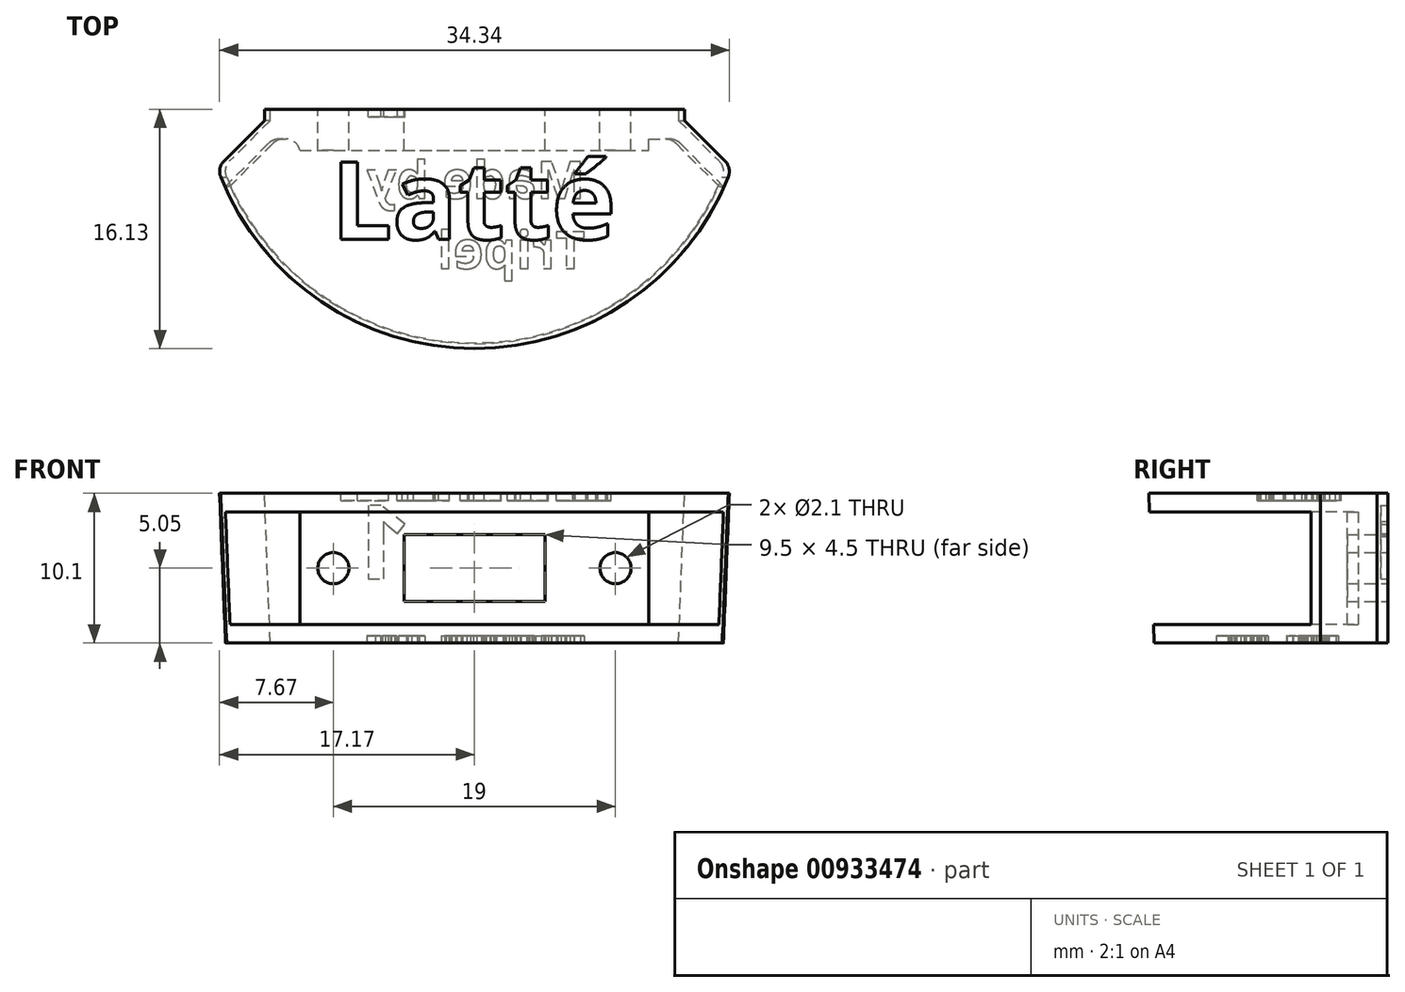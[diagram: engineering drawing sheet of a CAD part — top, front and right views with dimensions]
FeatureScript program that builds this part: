
annotation { "Feature Type Name" : "Feature", "Feature Type Description" : "" }
export const myFeature = defineFeature(function(context is Context, id is Id, definition is map)
    precondition{}
    {
        {
            assignVariable(context, id + "F0", {"variableType" : VariableType.LENGTH, "name" : "SwitchW", "lengthValue" : 7.6 * mm});
        }
        {
            assignVariable(context, id + "F1", {"variableType" : VariableType.LENGTH, "name" : "TopT", "lengthValue" : 2 * mm});
        }
        {
            assignVariable(context, id + "F2", {"variableType" : VariableType.LENGTH, "name" : "SideT", "lengthValue" : 1.25 * mm});
        }
        {
            var Q0;
            Q0=qCreatedBy(makeId("Top.planeOp"),FACE);
            var sketch = newSketch(context, id + "F3", { "sketchPlane" : qUnion([Q0])});
            skLineSegment(sketch, "E0", {"start": v(-13.75, 0) * mm, "end": v(13.75, 0) * mm});
            skPoint(sketch, "E1", {"position": v(0, 0) * mm});
            skLineSegment(sketch, "E2", {"start": v(-13.75, 0) * mm, "end": v(-16.93, -3.18) * mm});
            skLineSegment(sketch, "E3", {"start": v(13.75, 0) * mm, "end": v(16.93, -3.18) * mm});
            skArc(sketch, "E4", {"start": v(-16.93, -3.18) * mm, "mid": v(0, -15) * mm, "end": v(16.93, -3.18) * mm});
            skSolve(sketch);
        }
        {
            var Q0;
            Q0=qCreatedBy(makeId("Top.planeOp"),FACE);
            cPlane(context, id + "F4", {"entities" : qUnion([Q0]), "cplaneType" : CPlaneType.OFFSET, "offset" : getVariable(context, 'SwitchW') + (2 * getVariable(context, 'SideT')), "width" : 150 * mm, "height" : 150 * mm});
        }
        {
            var Q0;
            Q0=qCreatedBy(id+"F4.planeOp",FACE);
            var sketch = newSketch(context, id + "F5", { "sketchPlane" : qUnion([Q0])});
            skLineSegment(sketch, "E5.0", {"start": v(-14.15, 0) * mm, "end": v(14.15, 0) * mm});
            skLineSegment(sketch, "E6", {"start": v(-14.15, 0) * mm, "end": v(-17.33, -3.18) * mm});
            skLineSegment(sketch, "E7", {"start": v(14.15, 0) * mm, "end": v(17.33, -3.18) * mm});
            skArc(sketch, "E8.0", {"start": v(-16.93, -3.18) * mm, "mid": v(0, -15) * mm, "end": v(16.93, -3.18) * mm, "construction": true});
            skArc(sketch, "E9.0", {"start": v(-17.33, -3.18) * mm, "mid": v(0, -15.38) * mm, "end": v(17.33, -3.18) * mm});
            skSolve(sketch);
        }
        {
            var Q0;
            Q0 = qSketchRegion(id + "F3", true);
            var Q1;
            Q1 = qSketchRegion(id + "F5", true);
            loft(context, id + "F6", {"sheetProfilesArray" : [{ "sheetProfileEntities" : qUnion([Q0]) }, { "sheetProfileEntities" : qUnion([Q1]) }]});
        }
        {
            var Q0;
            Q0=makeQuery(id+"F6.opLoft","SWEPT_FACE",FACE,{"disambiguationData":[OSD([sQuery(id+"F3.wireOp",EDGE,"E2"),sQuery(id+"F3.wireOp",EDGE,"E3"),sQuery(id+"F3.wireOp",EDGE,"E4"),sQuery(id+"F5.wireOp",EDGE,"E6"),sQuery(id+"F5.wireOp",EDGE,"E7"),sQuery(id+"F5.wireOp",EDGE,"E9.0")])]});
            shell(context, id + "F7", {"entities" : qUnion([Q0]), "thickness" : getVariable(context, 'SideT')});
        }
        {
            var Q0;
            Q0=makeQuery(id+"F7.opShell","OFFSET_FACE",FACE,{"disambiguationData":[OSD([sQuery(id+"F3.wireOp",EDGE,"E0"),sQuery(id+"F3.wireOp",EDGE,"E2"),sQuery(id+"F3.wireOp",EDGE,"E3"),sQuery(id+"F5.wireOp",EDGE,"E5.0"),sQuery(id+"F5.wireOp",EDGE,"E6"),sQuery(id+"F5.wireOp",EDGE,"E7")])]});
            var sketch = newSketch(context, id + "F8", { "sketchPlane" : qUnion([Q0])});
            skLineSegment(sketch, "E10.0", {"start": v(11.75, 1.25) * mm, "end": v(-11.75, 1.25) * mm});
            skLineSegment(sketch, "E11.0", {"start": v(11.75, 8.85) * mm, "end": v(-11.75, 8.85) * mm});
            skPoint(sketch, "E12.orphan", {"position": v(-13.58, 8.85) * mm});
            skPoint(sketch, "E13.orphan", {"position": v(-14.15, 10.1) * mm});
            skPoint(sketch, "E14.orphan", {"position": v(-13.28, 1.25) * mm});
            skPoint(sketch, "E15.orphan", {"position": v(-13.75, 0) * mm});
            skPoint(sketch, "E16.orphan", {"position": v(13.58, 8.85) * mm});
            skPoint(sketch, "E17.orphan", {"position": v(14.15, 10.1) * mm});
            skPoint(sketch, "E18.orphan", {"position": v(13.28, 1.25) * mm});
            skPoint(sketch, "E19.orphan", {"position": v(13.75, 0) * mm});
            skPoint(sketch, "E20", {"position": v(0, 1.25) * mm});
            skLineSegment(sketch, "E21", {"start": v(-11.75, 1.25) * mm, "end": v(-11.75, 8.85) * mm});
            skLineSegment(sketch, "E22", {"start": v(11.75, 8.85) * mm, "end": v(11.75, 1.25) * mm});
            skSolve(sketch);
        }
        {
            var Q0;
            Q0 = qSketchRegion(id + "F8", true);
            extrude(context, id + "F9", {"entities" : qUnion([Q0]), "operationType" : NewBodyOperationType.ADD, "depth" : getVariable(context, 'TopT') - getVariable(context, 'SideT'), "offsetDistance" : 25 * mm});
        }
        {
            var Q0;
            Q0=makeQuery(id+"F6.opLoft","SWEPT_FACE",FACE,{"disambiguationData":[OSD([sQuery(id+"F3.wireOp",EDGE,"E0"),sQuery(id+"F3.wireOp",EDGE,"E2"),sQuery(id+"F3.wireOp",EDGE,"E3"),sQuery(id+"F5.wireOp",EDGE,"E5.0"),sQuery(id+"F5.wireOp",EDGE,"E6"),sQuery(id+"F5.wireOp",EDGE,"E7")])]});
            var sketch = newSketch(context, id + "F10", { "sketchPlane" : qUnion([Q0])});
            skLineSegment(sketch, "E23.0", {"start": v(-13.75, 0) * mm, "end": v(-14.15, 10.1) * mm});
            skLineSegment(sketch, "E24.0", {"start": v(-14.15, 10.1) * mm, "end": v(14.15, 10.1) * mm});
            skLineSegment(sketch, "E25.0", {"start": v(-13.75, 0) * mm, "end": v(13.75, 0) * mm});
            skLineSegment(sketch, "E26.0", {"start": v(13.75, 0) * mm, "end": v(14.15, 10.1) * mm});
            skSolve(sketch);
        }
        {
            var Q0;
            Q0 = qSketchRegion(id + "F10", true);
            extrude(context, id + "F11", {"entities" : qUnion([Q0]), "operationType" : NewBodyOperationType.ADD, "depth" : getVariable(context, 'TopT') - getVariable(context, 'SideT'), "offsetDistance" : 25 * mm});
        }
        {
            var Q0;
            Q0=makeQuery(id+"F11.opExtrude","CAP_FACE",FACE,{"disambiguationData":[OSD([sQuery(id+"F10.wireOp",EDGE,"E23.0"),sQuery(id+"F10.wireOp",EDGE,"E24.0"),sQuery(id+"F10.wireOp",EDGE,"E25.0"),sQuery(id+"F10.wireOp",EDGE,"E26.0")])],"isStart":false});
            var sketch = newSketch(context, id + "F12", { "sketchPlane" : qUnion([Q0])});
            skLineSegment(sketch, "E27", {"start": v(0, -3.67) * mm, "end": v(0, 15.19) * mm, "construction": true});
            skLineSegment(sketch, "E28", {"start": v(20.07, 5.05) * mm, "end": v(-20.07, 5.05) * mm, "construction": true});
            skPoint(sketch, "E29", {"position": v(15.32, 5.05) * mm});
            skCircle(sketch, "E30", {"center": v(9.5, 5.05) * mm, "radius": 1.05 * mm});
            skCircle(sketch, "E31", {"center": v(-9.5, 5.05) * mm, "radius": 1.05 * mm});
            skLineSegment(sketch, "E32.bottom", {"start": v(4.75, 7.3) * mm, "end": v(-4.75, 7.3) * mm});
            skLineSegment(sketch, "E32.top", {"start": v(4.75, 2.8) * mm, "end": v(-4.75, 2.8) * mm});
            skLineSegment(sketch, "E32.left", {"start": v(4.75, 7.3) * mm, "end": v(4.75, 2.8) * mm});
            skLineSegment(sketch, "E32.right", {"start": v(-4.75, 7.3) * mm, "end": v(-4.75, 2.8) * mm});
            skPoint(sketch, "E32.middle", {"position": v(0, 5.05) * mm});
            skPoint(sketch, "E32.middle.positionSnap0", {"position": v(0, 5.05) * mm});
            skPoint(sketch, "E32.centerSnap0", {"position": v(0, 5.05) * mm});
            skPoint(sketch, "E33", {"position": v(-13.95, 5.05) * mm});
            skSolve(sketch);
        }
        {
            var Q0;
            Q0 = qSketchRegion(id + "F12", true);
            var Q1;
            Q1=makeQuery(id+"F9.opExtrude","CAP_FACE",FACE,{"disambiguationData":[OSD([sQuery(id+"F8.wireOp",EDGE,"E10.0"),sQuery(id+"F8.wireOp",EDGE,"E11.0"),sQuery(id+"F8.wireOp",EDGE,"15eb3aa8-44bb-4b64-87c7-f76767814951.0"),sQuery(id+"F8.wireOp",EDGE,"fdead475-6918-48d0-8872-fc0451bcf777.0")])],"isStart":false});
            extrude(context, id + "F13", {"entities" : qUnion([Q0]), "operationType" : NewBodyOperationType.REMOVE, "endBound" : BoundingType.UP_TO_SURFACE, "oppositeDirection" : true, "depth" : 25 * mm, "endBoundEntityFace" : qUnion([Q1]), "offsetDistance" : 25 * mm});
        }
        {
            var Q0;
            Q0=makeQuery(id+"F11.opExtrude","CAP_FACE",FACE,{"disambiguationData":[OSD([sQuery(id+"F10.wireOp",EDGE,"E23.0"),sQuery(id+"F10.wireOp",EDGE,"E24.0"),sQuery(id+"F10.wireOp",EDGE,"E25.0"),sQuery(id+"F10.wireOp",EDGE,"E26.0")])],"isStart":false});
            var sketch = newSketch(context, id + "F14", { "sketchPlane" : qUnion([Q0])});
            skText(sketch, "E34", { "text": "1", "fontName": "NotoSans-Bold.ttf"});
            const initialGuessF14  = {"E34": [0.00427, 0.00433, 1, 0, 0.005]};
            skSetInitialGuess(sketch, initialGuessF14);
            skSolve(sketch);
        }
        {
            var Q0;
            Q0 = qSketchRegion(id + "F14", true);
            extrude(context, id + "F15", {"entities" : qUnion([Q0]), "operationType" : NewBodyOperationType.REMOVE, "oppositeDirection" : true, "depth" : 0.5 * mm, "offsetDistance" : 25 * mm});
        }
        {
            var Q0;
            Q0=makeQuery(id+"F6.opLoft","CAP_FACE",FACE,{"disambiguationData":[OSD([makeQuery(id+"F3.imprint","IMPRINT",FACE,{"disambiguationData":[TD([[makeQuery(id+"F3.imprint","IMPRINT",EDGE,{"derivedFrom":sQuery(id+"F3.wireOp",EDGE,"E0")}),-1.0]])]})])],"isStart":true});
            var sketch = newSketch(context, id + "F16", { "sketchPlane" : qUnion([Q0])});
            skText(sketch, "E35", { "text": "Made by\nTripel", "fontName": "OpenSans-Bold.ttf"});
            const initialGuessF16  = {"E35": [0.00746, 0.00525, -1, 0, 0.0025]};
            skSetInitialGuess(sketch, initialGuessF16);
            skSolve(sketch);
        }
        {
            var Q0;
            Q0 = qSketchRegion(id + "F16", true);
            extrude(context, id + "F17", {"entities" : qUnion([Q0]), "operationType" : NewBodyOperationType.REMOVE, "oppositeDirection" : true, "depth" : 0.5 * mm, "offsetDistance" : 25 * mm});
        }
        {
            var Q0;
            Q0=makeQuery(id+"F6.opLoft","SWEPT_EDGE",EDGE,{"disambiguationData":[OSD([sQuery(id+"F3.wireOp",EDGE,"E3"),sQuery(id+"F3.wireOp",EDGE,"E4"),sQuery(id+"F5.wireOp",EDGE,"E7"),sQuery(id+"F5.wireOp",EDGE,"E9.0")])]});
            var Q1;
            Q1=makeQuery(id+"F6.opLoft","SWEPT_EDGE",EDGE,{"disambiguationData":[OSD([sQuery(id+"F3.wireOp",EDGE,"E2"),sQuery(id+"F3.wireOp",EDGE,"E4"),sQuery(id+"F5.wireOp",EDGE,"E6"),sQuery(id+"F5.wireOp",EDGE,"E9.0")])]});
            fillet(context, id + "F18", {"entities" : qUnion([Q0, Q1]), "radius" : 1 * mm, "tangentPropagation" : true, "allowEdgeOverflow" : false});
        }
        {
            var Q0;
            Q0=makeQuery(id+"F7.opShell","OFFSET_EDGE",EDGE,{"disambiguationData":[OSD([sQuery(id+"F3.wireOp",EDGE,"E0"),sQuery(id+"F3.wireOp",EDGE,"E2"),sQuery(id+"F5.wireOp",EDGE,"E5.0"),sQuery(id+"F5.wireOp",EDGE,"E6")])]});
            var Q1;
            Q1=makeQuery(id+"F9.opExtrude","CAP_EDGE",EDGE,{"disambiguationData":[OSD([sQuery(id+"F8.wireOp",EDGE,"E21")])],"isStart":true});
            var Q2;
            Q2=makeQuery(id+"F9.opExtrude","CAP_EDGE",EDGE,{"disambiguationData":[OSD([sQuery(id+"F8.wireOp",EDGE,"E22")])],"isStart":true});
            var Q3;
            Q3=makeQuery(id+"F7.opShell","OFFSET_EDGE",EDGE,{"disambiguationData":[OSD([sQuery(id+"F3.wireOp",EDGE,"E0"),sQuery(id+"F3.wireOp",EDGE,"E3"),sQuery(id+"F5.wireOp",EDGE,"E5.0"),sQuery(id+"F5.wireOp",EDGE,"E7")])]});
            fillet(context, id + "F19", {"entities" : qUnion([Q0, Q1, Q2, Q3]), "radius" : 1 * mm, "tangentPropagation" : true, "allowEdgeOverflow" : false});
        }
        {
            var Q0;
            Q0=makeQuery(id+"F11.boolean.opBoolean","MERGE",FACE,{"derivedFrom":[makeQuery(id+"F6.opLoft","CAP_FACE",FACE,{"disambiguationData":[OSD([makeQuery(id+"F5.imprint","IMPRINT",FACE,{"disambiguationData":[TD([[makeQuery(id+"F5.imprint","IMPRINT",EDGE,{"derivedFrom":sQuery(id+"F5.wireOp",EDGE,"E5.0")}),-1.0]])]})])],"isStart":true}),makeQuery(id+"F11.opExtrude","SWEPT_FACE",FACE,{"disambiguationData":[OSD([sQuery(id+"F10.wireOp",EDGE,"E24.0")])]})]});
            var sketch = newSketch(context, id + "F20", { "sketchPlane" : qUnion([Q0])});
            skText(sketch, "E36", { "text": "Latté", "fontName": "OpenSans-Bold.ttf"});
            const initialGuessF20  = {"E36": [-0.00965, -0.008, 1, 0, 0.00525]};
            skSetInitialGuess(sketch, initialGuessF20);
            skSolve(sketch);
        }
        {
            var Q0;
            Q0 = qSketchRegion(id + "F20", true);
            extrude(context, id + "F21", {"entities" : qUnion([Q0]), "operationType" : NewBodyOperationType.REMOVE, "oppositeDirection" : true, "depth" : 0.5 * mm, "offsetDistance" : 25 * mm});
        }
    });
